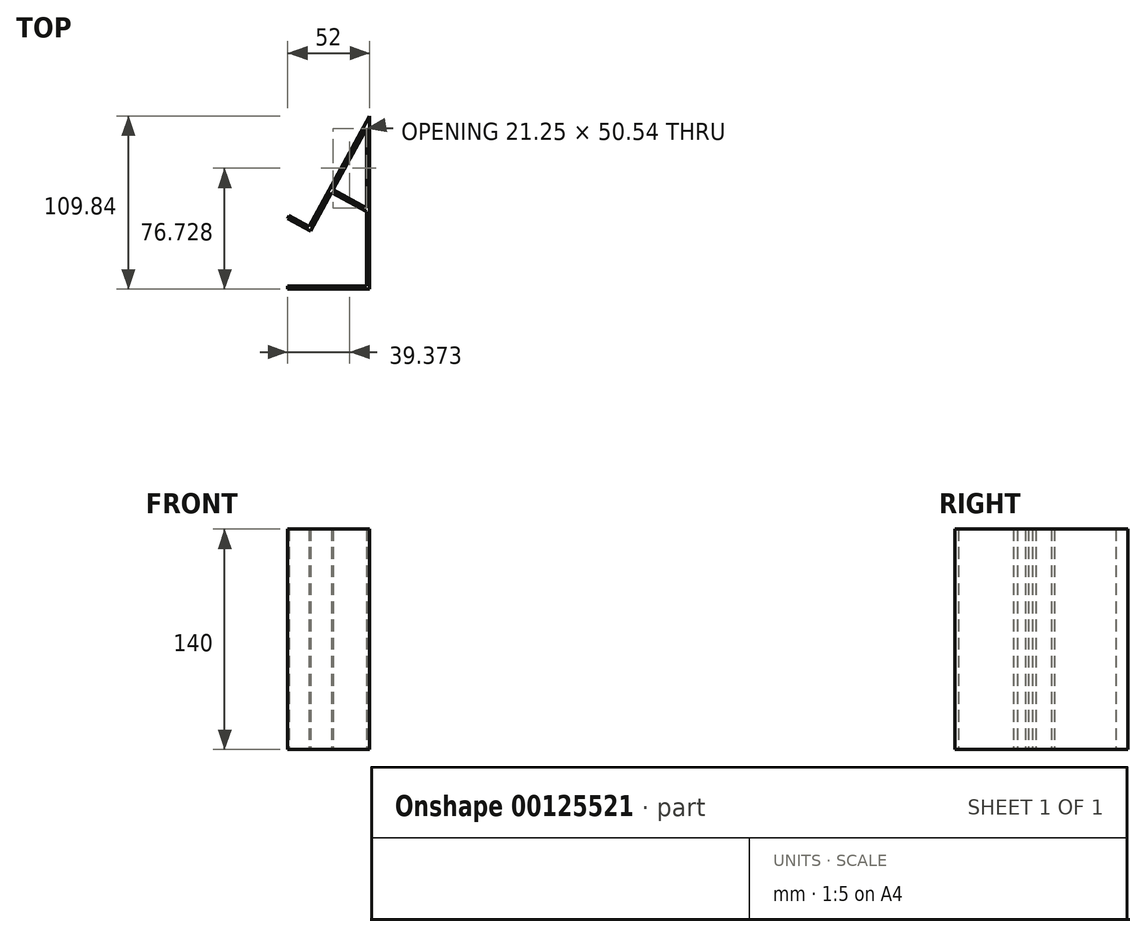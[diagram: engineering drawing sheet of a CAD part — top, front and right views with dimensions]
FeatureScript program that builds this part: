
annotation { "Feature Type Name" : "Feature", "Feature Type Description" : "" }
export const myFeature = defineFeature(function(context is Context, id is Id, definition is map)
    precondition{}
    {
        {
            var Q0;
            Q0=qCreatedBy(makeId("Top.planeOp"),FACE);
            var sketch = newSketch(context, id + "F0", { "sketchPlane" : qUnion([Q0])});
            skLineSegment(sketch, "E0", {"start": v(0, 0) * mm, "end": v(0, 100) * mm});
            skLineSegment(sketch, "E1", {"start": v(0, 0) * mm, "end": v(-50, 0) * mm});
            skLineSegment(sketch, "E2", {"start": v(0, 100) * mm, "end": v(-35.52, 34.9) * mm});
            skLineSegment(sketch, "E3", {"start": v(-35.52, 34.9) * mm, "end": v(-50, 42.8) * mm});
            skLineSegment(sketch, "E4", {"start": v(-50, 42.8) * mm, "end": v(-49.04, 44.56) * mm});
            skLineSegment(sketch, "E5", {"start": v(-49.04, 44.56) * mm, "end": v(-36.32, 37.62) * mm});
            skLineSegment(sketch, "E6", {"start": v(-50, 0) * mm, "end": v(-50, -2) * mm});
            skLineSegment(sketch, "E7", {"start": v(-50, -2) * mm, "end": v(2, -2) * mm});
            skLineSegment(sketch, "E8", {"start": v(2, -2) * mm, "end": v(2, 107.84) * mm});
            skLineSegment(sketch, "E9", {"start": v(-36.32, 37.62) * mm, "end": v(2, 107.84) * mm});
            skLineSegment(sketch, "E10", {"start": v(0, 49.46) * mm, "end": v(-21.25, 61.05) * mm});
            skLineSegment(sketch, "E11", {"start": v(-21.25, 61.05) * mm, "end": v(-21.25, 61.05) * mm});
            skLineSegment(sketch, "E12", {"start": v(-22.21, 59.3) * mm, "end": v(0, 47.18) * mm});
            skSolve(sketch);
        }
        {
            var Q0;
            {var subQ1=sQuery(id+"F0.wireOp",EDGE,"E1");Q0=makeQuery(id+"F0.imprint","IMPRINT",FACE,{"disambiguationData":[TD([[makeQuery(id+"F0.imprint","IMPRINT",EDGE,{"derivedFrom":subQ1}),1.0]])]});}
            var Q1;
            {var subQ0=sQuery(id+"F0.wireOp",EDGE,"E10");Q1=makeQuery(id+"F0.imprint","IMPRINT",FACE,{"disambiguationData":[TD([[makeQuery(id+"F0.imprint","IMPRINT",EDGE,{"derivedFrom":subQ0}),1.0]])]});}
            extrude(context, id + "F1", {"entities" : qUnion([Q0, Q1]), "depth" : 140 * mm});
        }
    });
